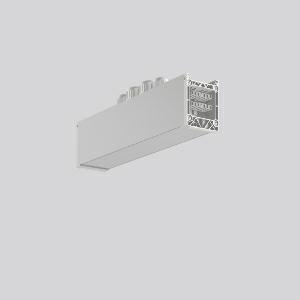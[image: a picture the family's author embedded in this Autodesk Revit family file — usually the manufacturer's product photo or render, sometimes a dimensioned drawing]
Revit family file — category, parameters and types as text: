
# Revit family: linedo_mitteleinspeisung_14pol_b_b_982698_000_1_3654
name_source: partatom
category: Lighting Fixtures
units: mm (PartAtom-declared; Revit-internal decimal feet)

## family parameters
Cut with Voids When Loaded = No
Host = Face
Light Source = No
Part Type = Normal
Room Calculation Point = No
Round Connector Dimension = Use Diameter
Shared = No

## types (1)
- LINEDO_Mitteleinspeisung_14pol_B_B
    Apparent Load = 0 VA
    Default Elevation = 1800 mm
    Description = Series: LINEDO
Middle power feed, 14-pole, connection socket / socket. Housing: extruded aluminium profile, anodised. Cover made of plastic, surface like housing. LINEDO plug system, plastic, light grey. 4 cable glands (2 x M20 and 2 x M25). Cable glands on top. Easy connection for rigid or flexible wires.
Colour: anodised aluminium
Length: 312 mm
Width: 58 mm
Height: 76 mm
Weight: 850 g
    Height = 76 mm
    Lamp = 0 x
    Length = 312 mm
    Luminous efficacy = 0 lm/W
    Manufacturer = RZB
    ModVariant = No
    Model = 982698.000.1
    Mounting Place = Ceiling
    Mounting Type = Pendant, Surface mounted
    Number of Poles = 1
    OnlyDefault = Yes
    Power Factor = 1
    Product Name = LINEDO_Mitteleinspeisung_14pol_B_B
    Product group = Surface mounted continuous line luminaire system
    ProductGroupID = 310
    Protection Class = Protection class I
    Protection Degree = IP 54
    RLX_Detail_Level = 1
    RLX_Emergency_Light_Flux = 0 lm
    RLX_Emergency_Type = 0
    RLX_Emergency_Type_DB = No
    RlxData = <blob elided: 22025 chars, md5=0e9c41b6>
    Standby Power = 0 W
    System Light Flux = 0 lm
    System Power = 0 W
    Type Comments = Product without accessories
    Type Image = 982698.000.1.jpg
    URL = http://relux.com
    VarID = ---
    Voltage = 0 V
    Weight = 0.00 kg
    Width = 58 mm

## geometry (parser evidence)
native form markers: Blend x4, Sweep x12
no freeform markers — native parametric forms only
